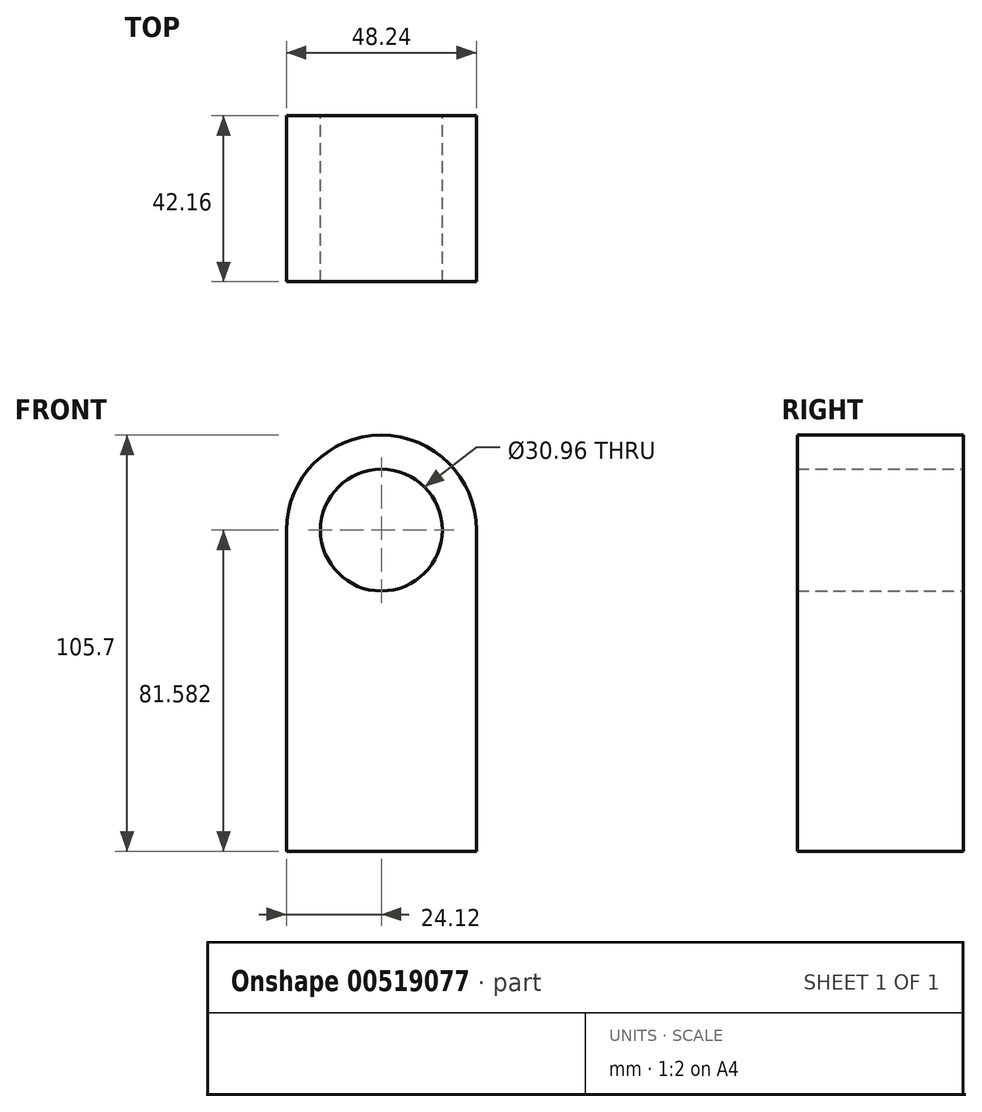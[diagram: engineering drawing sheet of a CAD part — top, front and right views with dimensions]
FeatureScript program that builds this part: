
annotation { "Feature Type Name" : "Feature", "Feature Type Description" : "" }
export const myFeature = defineFeature(function(context is Context, id is Id, definition is map)
    precondition{}
    {
        {
            var Q0;
            Q0=qCreatedBy(makeId("Front.planeOp"),FACE);
            var sketch = newSketch(context, id + "F0", { "sketchPlane" : qUnion([Q0])});
            skLineSegment(sketch, "E0.bottom", {"start": v(24.12, 40.8) * mm, "end": v(-24.12, 40.8) * mm});
            skLineSegment(sketch, "E0.top", {"start": v(24.12, -40.8) * mm, "end": v(-24.12, -40.8) * mm});
            skLineSegment(sketch, "E0.left", {"start": v(24.12, 40.8) * mm, "end": v(24.12, -40.8) * mm});
            skLineSegment(sketch, "E0.right", {"start": v(-24.12, 40.8) * mm, "end": v(-24.12, -40.8) * mm});
            skPoint(sketch, "E0.middle", {"position": v(0, 0) * mm});
            skCircle(sketch, "E1", {"center": v(0, 40.8) * mm, "radius": 24.12 * mm});
            skCircle(sketch, "E2.0", {"center": v(0, 40.8) * mm, "radius": 15.48 * mm});
            skSolve(sketch);
        }
        {
            var Q0;
            Q0=makeQuery(id+"F0.imprint","IMPRINT",FACE,{"disambiguationData":[TD([[makeQuery(id+"F0.imprint","IMPRINT",EDGE,{"derivedFrom":sQuery(id+"F0.wireOp",EDGE,"E0.top")}),-1.0]])]});
            var Q1;
            {var subQ1=sQuery(id+"F0.wireOp",EDGE,"E0.bottom");var subQ3=sQuery(id+"F0.wireOp",EDGE,"E2.0");var subQ4=makeQuery(id+"F0.imprint","INTERSECT",VERTEX,{"disambiguationData":[OD(0.0)],"derivedFrom":[subQ1,subQ3]});Q1=makeQuery(id+"F0.imprint","IMPRINT",FACE,{"disambiguationData":[TD([[makeQuery(id+"F0.imprint","IMPRINT",EDGE,{"disambiguationData":[TD([[subQ4,1.0]])],"derivedFrom":subQ3}),-1.0]])]});}
            var Q2;
            {var subQ1=sQuery(id+"F0.wireOp",EDGE,"E0.bottom");var subQ3=sQuery(id+"F0.wireOp",EDGE,"E2.0");var subQ4=makeQuery(id+"F0.imprint","INTERSECT",VERTEX,{"disambiguationData":[OD(0.0)],"derivedFrom":[subQ1,subQ3]});Q2=makeQuery(id+"F0.imprint","IMPRINT",FACE,{"disambiguationData":[TD([[makeQuery(id+"F0.imprint","IMPRINT",EDGE,{"disambiguationData":[TD([[subQ4,-1.0]])],"derivedFrom":subQ3}),-1.0]])]});}
            extrude(context, id + "F1", {"entities" : qUnion([Q0, Q1, Q2]), "depth" : 42.16 * mm});
        }
    });
